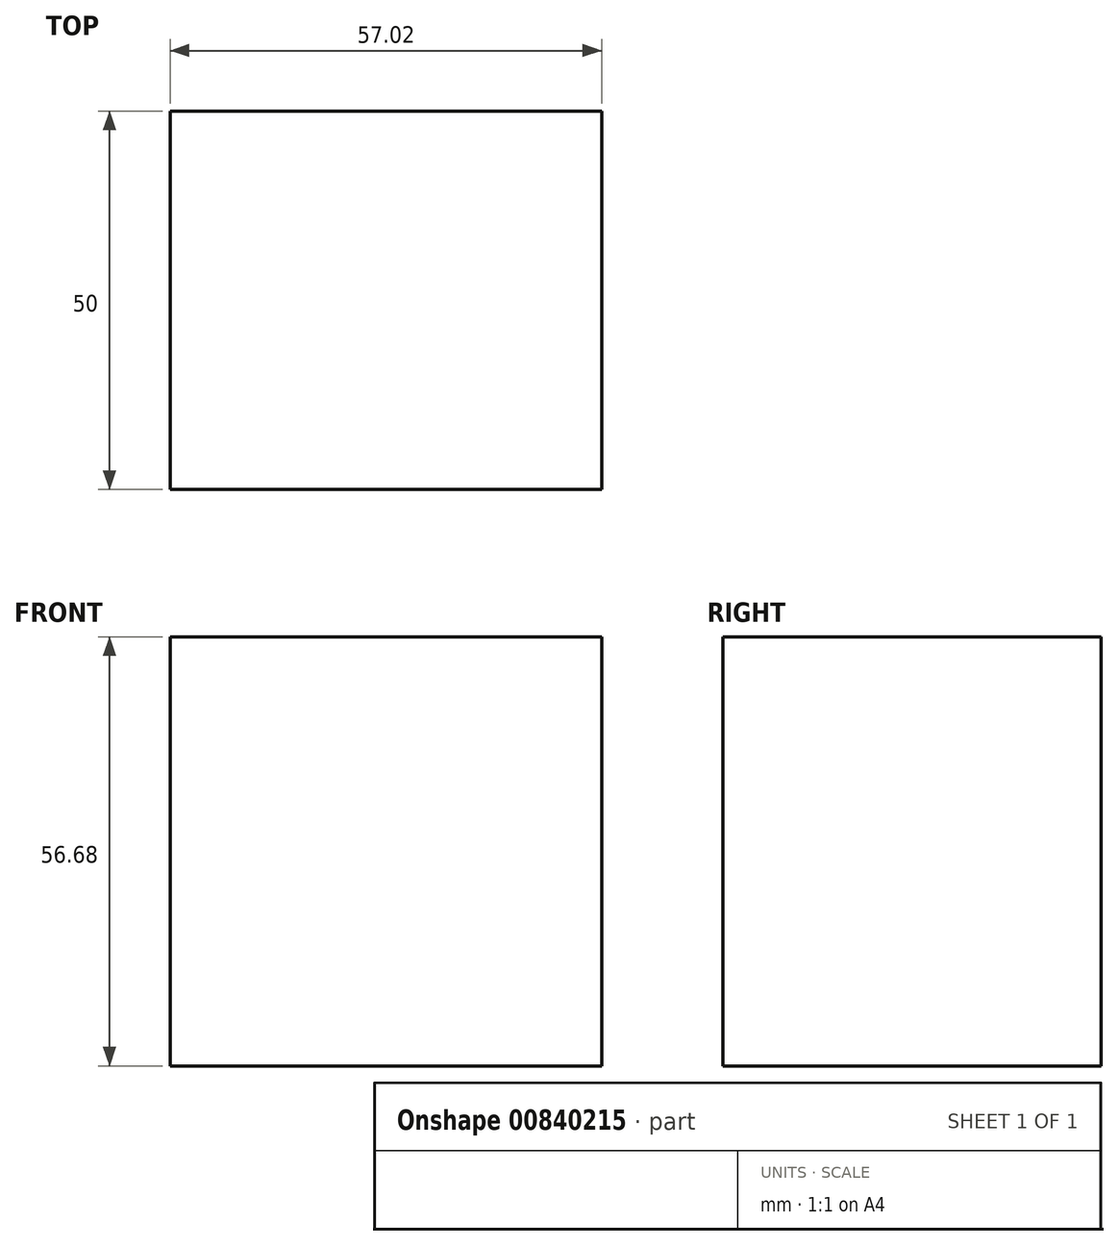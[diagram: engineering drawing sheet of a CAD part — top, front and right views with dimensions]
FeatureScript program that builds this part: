
annotation { "Feature Type Name" : "Feature", "Feature Type Description" : "" }
export const myFeature = defineFeature(function(context is Context, id is Id, definition is map)
    precondition{}
    {
        {
            var Q0;
            Q0=qCreatedBy(makeId("Front.planeOp"),FACE);
            var sketch = newSketch(context, id + "F0", { "sketchPlane" : qUnion([Q0])});
            skLineSegment(sketch, "E0.bottom", {"start": v(28.5, -28.34) * mm, "end": v(-28.5, -28.34) * mm});
            skLineSegment(sketch, "E0.top", {"start": v(28.5, 28.34) * mm, "end": v(-28.5, 28.34) * mm});
            skLineSegment(sketch, "E0.left", {"start": v(28.5, -28.34) * mm, "end": v(28.5, 28.34) * mm});
            skLineSegment(sketch, "E0.right", {"start": v(-28.5, -28.34) * mm, "end": v(-28.5, 28.34) * mm});
            skPoint(sketch, "E0.middle", {"position": v(0, 0) * mm});
            skSolve(sketch);
        }
        {
            var Q0;
            Q0=makeQuery(id+"F0.imprint","IMPRINT",FACE,{"disambiguationData":[TD([[makeQuery(id+"F0.imprint","IMPRINT",EDGE,{"derivedFrom":sQuery(id+"F0.wireOp",EDGE,"E0.bottom")}),-1.0]])]});
            var Q1;
            Q1 = qSketchRegion(id + "F0", true);
            extrude(context, id + "F1", {"entities" : qUnion([Q0, Q1]), "depth" : 50 * mm, "offsetDistance" : 25 * mm});
        }
    });
